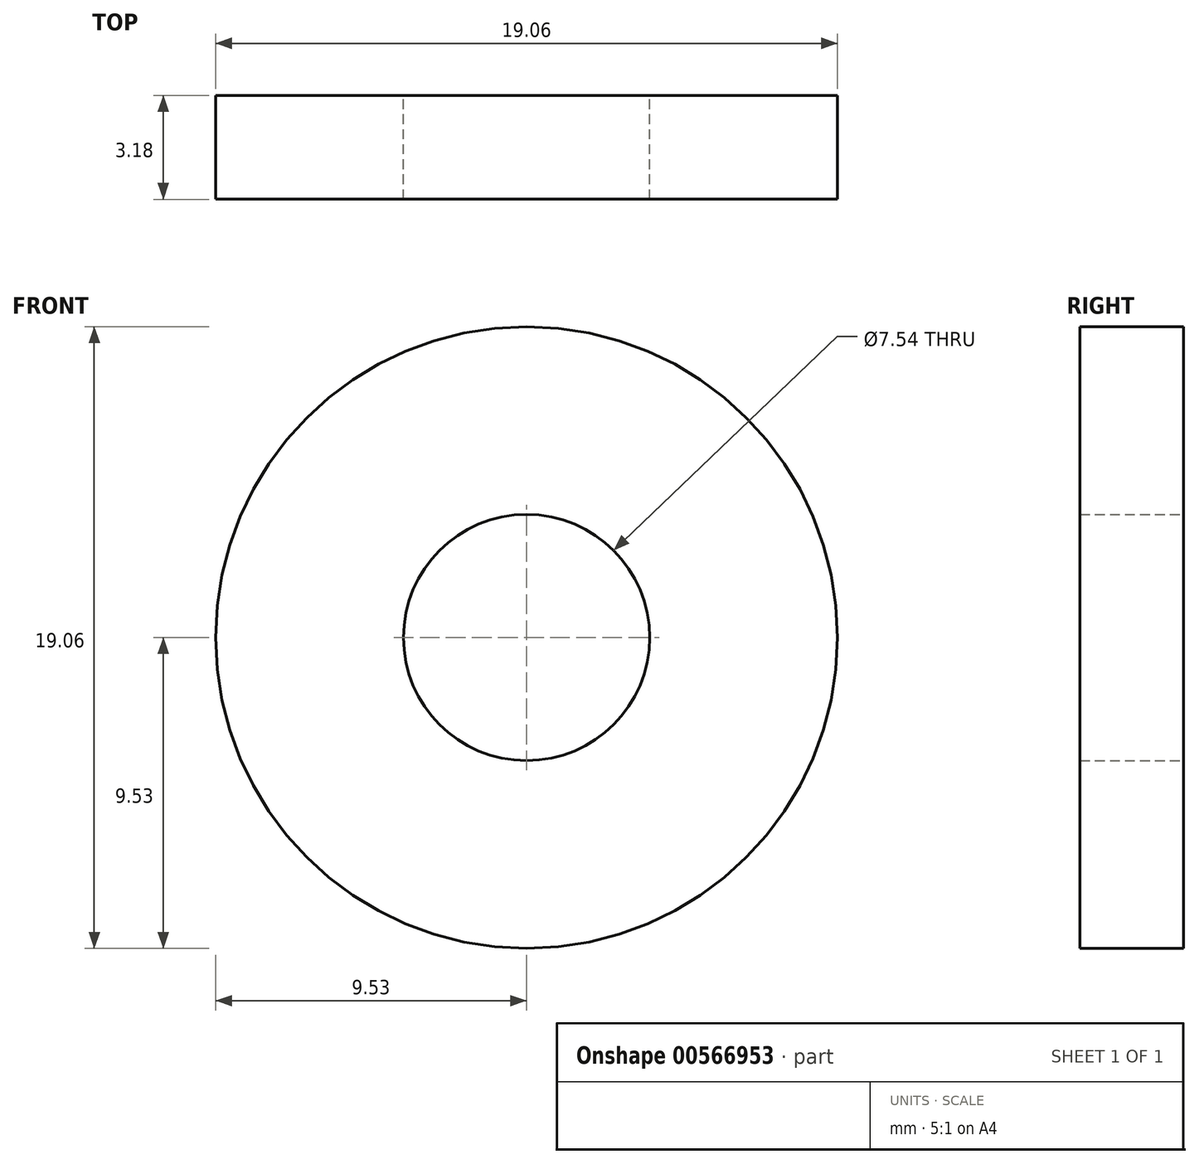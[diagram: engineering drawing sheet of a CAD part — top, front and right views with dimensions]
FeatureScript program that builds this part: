
annotation { "Feature Type Name" : "Feature", "Feature Type Description" : "" }
export const myFeature = defineFeature(function(context is Context, id is Id, definition is map)
    precondition{}
    {
        {
            var Q0;
            Q0=qCreatedBy(makeId("Front.planeOp"),FACE);
            var sketch = newSketch(context, id + "F0", { "sketchPlane" : qUnion([Q0])});
            skCircle(sketch, "E0", {"center": v(0, 0) * mm, "radius": 9.53 * mm});
            skCircle(sketch, "E1", {"center": v(0, 0) * mm, "radius": 3.77 * mm});
            skSolve(sketch);
        }
        {
            var Q0;
            Q0=makeQuery(id+"F0.imprint","IMPRINT",FACE,{"disambiguationData":[TD([[makeQuery(id+"F0.imprint","IMPRINT",EDGE,{"derivedFrom":sQuery(id+"F0.wireOp",EDGE,"E0")}),1.0]])]});
            extrude(context, id + "F1", {"entities" : qUnion([Q0]), "depth" : 3.17 * mm, "offsetDistance" : 25 * mm});
        }
    });
